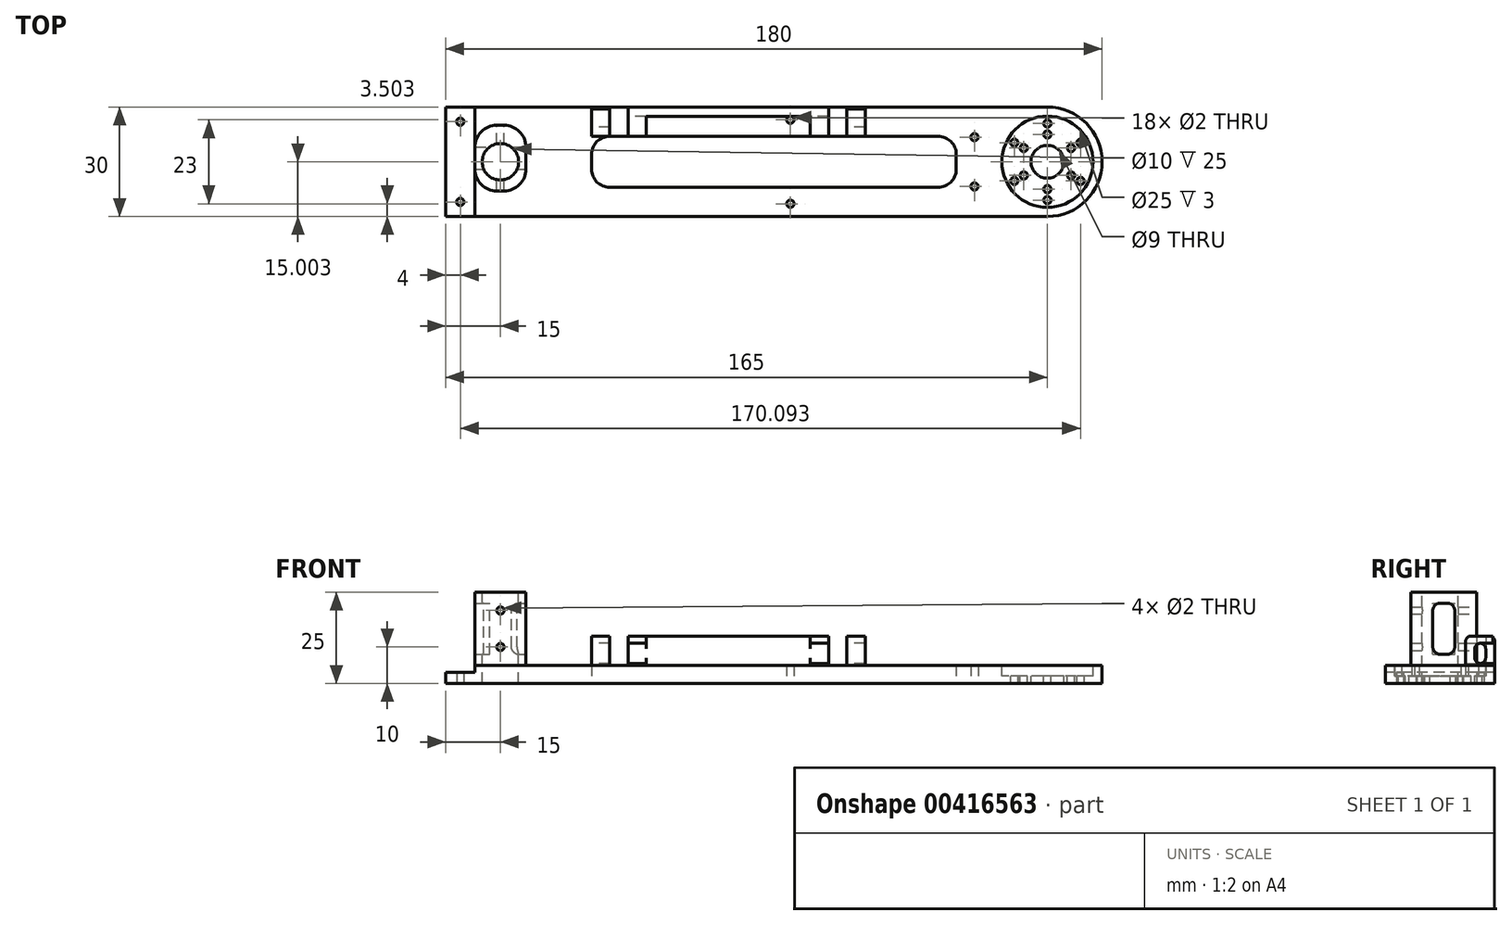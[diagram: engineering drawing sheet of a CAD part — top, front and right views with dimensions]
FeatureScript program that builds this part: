
annotation { "Feature Type Name" : "Feature", "Feature Type Description" : "" }
export const myFeature = defineFeature(function(context is Context, id is Id, definition is map)
    precondition{}
    {
        {
            var Q0;
            Q0=qCreatedBy(makeId("Top.planeOp"),FACE);
            var sketch = newSketch(context, id + "F0", { "sketchPlane" : qUnion([Q0])});
            skLineSegment(sketch, "E0.bottom", {"start": v(-80, 3.1) * mm, "end": v(100, 3.1) * mm});
            skLineSegment(sketch, "E0.top", {"start": v(-80, -26.9) * mm, "end": v(100, -26.9) * mm});
            skLineSegment(sketch, "E0.left", {"start": v(-80, 3.1) * mm, "end": v(-80, -26.9) * mm});
            skLineSegment(sketch, "E0.right", {"start": v(100, 3.1) * mm, "end": v(100, -26.9) * mm});
            skCircle(sketch, "E1", {"center": v(65, -5.15) * mm, "radius": 1 * mm});
            skCircle(sketch, "E2", {"center": v(65, -18.65) * mm, "radius": 1 * mm});
            skLineSegment(sketch, "E3.bottom", {"start": v(-40, -4.9) * mm, "end": v(60, -4.9) * mm});
            skLineSegment(sketch, "E3.top", {"start": v(-40, -18.9) * mm, "end": v(60, -18.9) * mm});
            skLineSegment(sketch, "E3.left", {"start": v(-40, -4.9) * mm, "end": v(-40, -18.9) * mm});
            skLineSegment(sketch, "E3.right", {"start": v(60, -4.9) * mm, "end": v(60, -18.9) * mm});
            skCircle(sketch, "E4", {"center": v(-76, -0.9) * mm, "radius": 1 * mm});
            skCircle(sketch, "E5", {"center": v(-76, -22.9) * mm, "radius": 1 * mm});
            skCircle(sketch, "E6", {"center": v(14.5, -23.4) * mm, "radius": 1 * mm});
            skCircle(sketch, "E7", {"center": v(14.5, -0.4) * mm, "radius": 1 * mm});
            skSolve(sketch);
        }
        {
            var Q0;
            Q0=makeQuery(id+"F0.imprint","IMPRINT",FACE,{"disambiguationData":[TD([[makeQuery(id+"F0.imprint","IMPRINT",EDGE,{"derivedFrom":sQuery(id+"F0.wireOp",EDGE,"E0.bottom")}),-1.0]])]});
            extrude(context, id + "F1", {"entities" : qUnion([Q0]), "depth" : 5 * mm});
        }
        {
            var Q0;
            Q0=makeQuery(id+"F1.opExtrude","CAP_FACE",FACE,{"disambiguationData":[OSD([sQuery(id+"F0.wireOp",EDGE,"E0.bottom"),sQuery(id+"F0.wireOp",EDGE,"E0.top"),sQuery(id+"F0.wireOp",EDGE,"E0.left"),sQuery(id+"F0.wireOp",EDGE,"E0.right")])],"isStart":false});
            var sketch = newSketch(context, id + "F2", { "sketchPlane" : qUnion([Q0])});
            skCircle(sketch, "E8", {"center": v(85, -11.9) * mm, "radius": 12.5 * mm});
            skCircle(sketch, "E9", {"center": v(85, -11.9) * mm, "radius": 4.5 * mm});
            skCircle(sketch, "E10", {"center": v(85, -4.4) * mm, "radius": 1 * mm});
            skCircle(sketch, "E11", {"center": v(85, -19.4) * mm, "radius": 1 * mm});
            skCircle(sketch, "E12", {"center": v(-65, -11.9) * mm, "radius": 5 * mm});
            skLineSegment(sketch, "E13.bottom", {"start": v(-72, -1.9) * mm, "end": v(-58, -1.9) * mm});
            skLineSegment(sketch, "E13.top", {"start": v(-72, -19.9) * mm, "end": v(-58, -19.9) * mm});
            skLineSegment(sketch, "E13.left", {"start": v(-72, -1.9) * mm, "end": v(-72, -19.9) * mm});
            skLineSegment(sketch, "E13.right", {"start": v(-58, -1.9) * mm, "end": v(-58, -19.9) * mm});
            skLineSegment(sketch, "E14.bottom", {"start": v(-80, 3.1) * mm, "end": v(-72, 3.1) * mm});
            skLineSegment(sketch, "E14.top", {"start": v(-80, -26.9) * mm, "end": v(-72, -26.9) * mm});
            skLineSegment(sketch, "E14.left", {"start": v(-80, 3.1) * mm, "end": v(-80, -26.9) * mm});
            skLineSegment(sketch, "E14.right", {"start": v(-72, 3.1) * mm, "end": v(-72, -26.9) * mm});
            skLineSegment(sketch, "E15", {"start": v(85, -11.9) * mm, "end": v(98.65, -11.9) * mm, "construction": true});
            skLineSegment(sketch, "E16", {"start": v(85, -11.9) * mm, "end": v(96.98, -4.98) * mm, "construction": true});
            skLineSegment(sketch, "E17", {"start": v(85, -11.9) * mm, "end": v(73.1, -5.02) * mm, "construction": true});
            skLineSegment(sketch, "E18", {"start": v(85, -11.9) * mm, "end": v(97.19, -18.93) * mm, "construction": true});
            skLineSegment(sketch, "E19", {"start": v(85, -11.9) * mm, "end": v(72.98, -18.84) * mm, "construction": true});
            skCircle(sketch, "E20", {"center": v(91.5, -8.15) * mm, "radius": 1 * mm});
            skCircle(sketch, "E21", {"center": v(91.5, -15.65) * mm, "radius": 1 * mm});
            skCircle(sketch, "E22", {"center": v(78.5, -15.65) * mm, "radius": 1 * mm});
            skCircle(sketch, "E23", {"center": v(78.5, -8.15) * mm, "radius": 1 * mm});
            skLineSegment(sketch, "E24", {"start": v(85, -11.9) * mm, "end": v(85, -25.3) * mm, "construction": true});
            skLineSegment(sketch, "E25", {"start": v(85, -11.9) * mm, "end": v(85, 1.9) * mm, "construction": true});
            skCircle(sketch, "E26", {"center": v(85, -1.4) * mm, "radius": 1 * mm});
            skCircle(sketch, "E27", {"center": v(85, -22.4) * mm, "radius": 1 * mm});
            skCircle(sketch, "E28", {"center": v(94.1, -17.15) * mm, "radius": 1 * mm});
            skCircle(sketch, "E29", {"center": v(94.1, -6.65) * mm, "radius": 1 * mm});
            skCircle(sketch, "E30", {"center": v(75.9, -6.65) * mm, "radius": 1 * mm});
            skCircle(sketch, "E31", {"center": v(75.9, -17.15) * mm, "radius": 1 * mm});
            skSolve(sketch);
        }
        {
            var Q0;
            Q0=makeQuery(id+"F2.imprint","IMPRINT",FACE,{"disambiguationData":[TD([[makeQuery(id+"F2.imprint","IMPRINT",EDGE,{"derivedFrom":sQuery(id+"F2.wireOp",EDGE,"E8")}),1.0]])]});
            extrude(context, id + "F3", {"entities" : qUnion([Q0]), "operationType" : NewBodyOperationType.REMOVE, "oppositeDirection" : true, "depth" : 3 * mm});
        }
        {
            var Q0;
            Q0=makeQuery(id+"F2.imprint","IMPRINT",FACE,{"disambiguationData":[TD([[makeQuery(id+"F2.imprint","IMPRINT",EDGE,{"derivedFrom":sQuery(id+"F2.wireOp",EDGE,"E9")}),1.0]])]});
            var Q1;
            Q1=makeQuery(id+"F2.imprint","IMPRINT",FACE,{"disambiguationData":[TD([[makeQuery(id+"F2.imprint","IMPRINT",EDGE,{"derivedFrom":sQuery(id+"F2.wireOp",EDGE,"E10")}),1.0]])]});
            var Q2;
            Q2=makeQuery(id+"F2.imprint","IMPRINT",FACE,{"disambiguationData":[TD([[makeQuery(id+"F2.imprint","IMPRINT",EDGE,{"derivedFrom":sQuery(id+"F2.wireOp",EDGE,"5qcmUWc9-dUiE-HqhH-y48y-BH5WIywJNnlC")}),1.0]])]});
            var Q3;
            Q3=makeQuery(id+"F2.imprint","IMPRINT",FACE,{"disambiguationData":[TD([[makeQuery(id+"F2.imprint","IMPRINT",EDGE,{"derivedFrom":sQuery(id+"F2.wireOp",EDGE,"E11")}),1.0]])]});
            var Q4;
            Q4=makeQuery(id+"F2.imprint","IMPRINT",FACE,{"disambiguationData":[TD([[makeQuery(id+"F2.imprint","IMPRINT",EDGE,{"derivedFrom":sQuery(id+"F2.wireOp",EDGE,"wZEUfmAI-Y2Ez-LQvS-xFHq-oZ12hOKPTyTT")}),1.0]])]});
            var Q5;
            Q5=makeQuery(id+"F2.imprint","IMPRINT",FACE,{"disambiguationData":[TD([[makeQuery(id+"F2.imprint","IMPRINT",EDGE,{"derivedFrom":sQuery(id+"F2.wireOp",EDGE,"E20")}),1.0]])]});
            var Q6;
            Q6=makeQuery(id+"F2.imprint","IMPRINT",FACE,{"disambiguationData":[TD([[makeQuery(id+"F2.imprint","IMPRINT",EDGE,{"derivedFrom":sQuery(id+"F2.wireOp",EDGE,"E21")}),1.0]])]});
            var Q7;
            Q7=makeQuery(id+"F2.imprint","IMPRINT",FACE,{"disambiguationData":[TD([[makeQuery(id+"F2.imprint","IMPRINT",EDGE,{"derivedFrom":sQuery(id+"F2.wireOp",EDGE,"E22")}),1.0]])]});
            var Q8;
            Q8=makeQuery(id+"F2.imprint","IMPRINT",FACE,{"disambiguationData":[TD([[makeQuery(id+"F2.imprint","IMPRINT",EDGE,{"derivedFrom":sQuery(id+"F2.wireOp",EDGE,"E23")}),1.0]])]});
            var Q9;
            Q9=makeQuery(id+"F2.imprint","IMPRINT",FACE,{"disambiguationData":[TD([[makeQuery(id+"F2.imprint","IMPRINT",EDGE,{"derivedFrom":sQuery(id+"F2.wireOp",EDGE,"E26")}),1.0]])]});
            var Q10;
            Q10=makeQuery(id+"F2.imprint","IMPRINT",FACE,{"disambiguationData":[TD([[makeQuery(id+"F2.imprint","IMPRINT",EDGE,{"derivedFrom":sQuery(id+"F2.wireOp",EDGE,"E30")}),1.0]])]});
            var Q11;
            Q11=makeQuery(id+"F2.imprint","IMPRINT",FACE,{"disambiguationData":[TD([[makeQuery(id+"F2.imprint","IMPRINT",EDGE,{"derivedFrom":sQuery(id+"F2.wireOp",EDGE,"E31")}),1.0]])]});
            var Q12;
            Q12=makeQuery(id+"F2.imprint","IMPRINT",FACE,{"disambiguationData":[TD([[makeQuery(id+"F2.imprint","IMPRINT",EDGE,{"derivedFrom":sQuery(id+"F2.wireOp",EDGE,"E27")}),1.0]])]});
            var Q13;
            Q13=makeQuery(id+"F2.imprint","IMPRINT",FACE,{"disambiguationData":[TD([[makeQuery(id+"F2.imprint","IMPRINT",EDGE,{"derivedFrom":sQuery(id+"F2.wireOp",EDGE,"E28")}),1.0]])]});
            var Q14;
            Q14=makeQuery(id+"F2.imprint","IMPRINT",FACE,{"disambiguationData":[TD([[makeQuery(id+"F2.imprint","IMPRINT",EDGE,{"derivedFrom":sQuery(id+"F2.wireOp",EDGE,"E29")}),1.0]])]});
            extrude(context, id + "F4", {"entities" : qUnion([Q0, Q1, Q2, Q3, Q4, Q5, Q6, Q7, Q8, Q9, Q10, Q11, Q12, Q13, Q14]), "operationType" : NewBodyOperationType.REMOVE, "oppositeDirection" : true, "depth" : 25 * mm, "offsetDistance" : 25 * mm});
        }
        {
            var Q0;
            Q0=makeQuery(id+"F1.opExtrude","SWEPT_EDGE",EDGE,{"disambiguationData":[OSD([sQuery(id+"F0.wireOp",EDGE,"E0.bottom"),sQuery(id+"F0.wireOp",EDGE,"E0.right")])]});
            var Q1;
            Q1=makeQuery(id+"F1.opExtrude","SWEPT_EDGE",EDGE,{"disambiguationData":[OSD([sQuery(id+"F0.wireOp",EDGE,"E0.top"),sQuery(id+"F0.wireOp",EDGE,"E0.right")])]});
            fillet(context, id + "F5", {"entities" : qUnion([Q0, Q1]), "radius" : 15 * mm, "tangentPropagation" : true, "allowEdgeOverflow" : false});
        }
        {
            var Q0;
            Q0=makeQuery(id+"F2.imprint","IMPRINT",FACE,{"disambiguationData":[TD([[makeQuery(id+"F2.imprint","IMPRINT",EDGE,{"derivedFrom":sQuery(id+"F2.wireOp",EDGE,"E12")}),1.0]])]});
            extrude(context, id + "F6", {"entities" : qUnion([Q0]), "operationType" : NewBodyOperationType.REMOVE, "oppositeDirection" : true, "depth" : 25 * mm});
        }
        {
            var Q0;
            Q0=makeQuery(id+"F1.opExtrude","SWEPT_EDGE",EDGE,{"disambiguationData":[OSD([sQuery(id+"F0.wireOp",EDGE,"E3.bottom"),sQuery(id+"F0.wireOp",EDGE,"E3.left")])]});
            var Q1;
            Q1=makeQuery(id+"F1.opExtrude","SWEPT_EDGE",EDGE,{"disambiguationData":[OSD([sQuery(id+"F0.wireOp",EDGE,"E3.top"),sQuery(id+"F0.wireOp",EDGE,"E3.left")])]});
            var Q2;
            Q2=makeQuery(id+"F1.opExtrude","SWEPT_EDGE",EDGE,{"disambiguationData":[OSD([sQuery(id+"F0.wireOp",EDGE,"E3.bottom"),sQuery(id+"F0.wireOp",EDGE,"E3.right")])]});
            var Q3;
            Q3=makeQuery(id+"F1.opExtrude","SWEPT_EDGE",EDGE,{"disambiguationData":[OSD([sQuery(id+"F0.wireOp",EDGE,"E3.top"),sQuery(id+"F0.wireOp",EDGE,"E3.right")])]});
            fillet(context, id + "F7", {"entities" : qUnion([Q0, Q1, Q2, Q3]), "radius" : 5 * mm, "tangentPropagation" : true, "allowEdgeOverflow" : false});
        }
        {
            var Q0;
            Q0=makeQuery(id+"F2.imprint","IMPRINT",FACE,{"disambiguationData":[TD([[makeQuery(id+"F2.imprint","IMPRINT",EDGE,{"derivedFrom":sQuery(id+"F2.wireOp",EDGE,"E12")}),-1.0]])]});
            extrude(context, id + "F8", {"entities" : qUnion([Q0]), "operationType" : NewBodyOperationType.ADD, "depth" : 20 * mm, "offsetDistance" : 25 * mm});
        }
        {
            var Q0;
            Q0=makeQuery(id+"F8.opExtrude","SWEPT_EDGE",EDGE,{"disambiguationData":[OSD([sQuery(id+"F2.wireOp",EDGE,"E13.top"),sQuery(id+"F2.wireOp",EDGE,"E13.left")])]});
            var Q1;
            Q1=makeQuery(id+"F8.opExtrude","SWEPT_EDGE",EDGE,{"disambiguationData":[OSD([sQuery(id+"F2.wireOp",EDGE,"E13.top"),sQuery(id+"F2.wireOp",EDGE,"E13.right")])]});
            var Q2;
            Q2=makeQuery(id+"F8.opExtrude","SWEPT_EDGE",EDGE,{"disambiguationData":[OSD([sQuery(id+"F2.wireOp",EDGE,"E13.bottom"),sQuery(id+"F2.wireOp",EDGE,"E13.left")])]});
            var Q3;
            Q3=makeQuery(id+"F8.opExtrude","SWEPT_EDGE",EDGE,{"disambiguationData":[OSD([sQuery(id+"F2.wireOp",EDGE,"E13.bottom"),sQuery(id+"F2.wireOp",EDGE,"E13.right")])]});
            fillet(context, id + "F9", {"entities" : qUnion([Q0, Q1, Q2, Q3]), "radius" : 6 * mm, "tangentPropagation" : true, "allowEdgeOverflow" : false});
        }
        {
            var Q0;
            {var subQ2=sQuery(id+"F2.wireOp",EDGE,"E14.bottom");Q0=makeQuery(id+"F2.imprint","IMPRINT",FACE,{"disambiguationData":[TD([[makeQuery(id+"F2.imprint","IMPRINT",EDGE,{"derivedFrom":subQ2}),-1.0]])]});}
            extrude(context, id + "F10", {"entities" : qUnion([Q0]), "operationType" : NewBodyOperationType.REMOVE, "oppositeDirection" : true, "depth" : 2 * mm, "offsetDistance" : 25 * mm});
        }
        {
            var Q0;
            Q0=makeQuery(id+"F8.opExtrude","SWEPT_FACE",FACE,{"disambiguationData":[OSD([sQuery(id+"F2.wireOp",EDGE,"E13.right")])]});
            var sketch = newSketch(context, id + "F11", { "sketchPlane" : qUnion([Q0])});
            skLineSegment(sketch, "E32.bottom", {"start": v(-13.9, 22) * mm, "end": v(-7.9, 22) * mm});
            skLineSegment(sketch, "E32.top", {"start": v(-13.9, 8) * mm, "end": v(-7.9, 8) * mm});
            skLineSegment(sketch, "E32.left", {"start": v(-13.9, 22) * mm, "end": v(-13.9, 8) * mm});
            skLineSegment(sketch, "E32.right", {"start": v(-7.9, 22) * mm, "end": v(-7.9, 8) * mm});
            skSolve(sketch);
        }
        {
            var Q0;
            Q0=makeQuery(id+"F11.imprint","IMPRINT",FACE,{"disambiguationData":[TD([[makeQuery(id+"F11.imprint","IMPRINT",EDGE,{"derivedFrom":sQuery(id+"F11.wireOp",EDGE,"E32.bottom")}),-1.0]])]});
            extrude(context, id + "F12", {"entities" : qUnion([Q0]), "operationType" : NewBodyOperationType.REMOVE, "oppositeDirection" : true, "depth" : 25 * mm, "offsetDistance" : 25 * mm});
        }
        {
            var Q0;
            {var subQ0=sQuery(id+"F2.wireOp",EDGE,"E13.right");var subQ1=sQuery(id+"F2.wireOp",EDGE,"E13.top");var subQ3=sQuery(id+"F11.wireOp",EDGE,"E32.top");var subQ4=sQuery(id+"F11.wireOp",EDGE,"E32.left");Q0=makeQuery(id+"F12.boolean.opBoolean","COPY",EDGE,{"disambiguationData":[TD([makeQuery(id+"F8.opExtrude","SWEPT_FACE",FACE,{"disambiguationData":[OSD([subQ0])]})])],"derivedFrom":makeQuery(id+"F12.opExtrude","SWEPT_EDGE",EDGE,{"disambiguationData":[OSD([subQ1,subQ0,subQ3,subQ4])]})});}
            var Q1;
            {var subQ0=sQuery(id+"F2.wireOp",EDGE,"E13.right");var subQ2=sQuery(id+"F2.wireOp",EDGE,"E13.bottom");var subQ3=sQuery(id+"F11.wireOp",EDGE,"E32.top");var subQ4=sQuery(id+"F11.wireOp",EDGE,"E32.right");Q1=makeQuery(id+"F12.boolean.opBoolean","COPY",EDGE,{"disambiguationData":[TD([makeQuery(id+"F8.opExtrude","SWEPT_FACE",FACE,{"disambiguationData":[OSD([subQ0])]})])],"derivedFrom":makeQuery(id+"F12.opExtrude","SWEPT_EDGE",EDGE,{"disambiguationData":[OSD([subQ2,subQ0,subQ3,subQ4])]})});}
            var Q2;
            {var subQ0=sQuery(id+"F2.wireOp",EDGE,"E13.right");var subQ2=sQuery(id+"F2.wireOp",EDGE,"E13.bottom");var subQ3=sQuery(id+"F11.wireOp",EDGE,"E32.bottom");var subQ4=sQuery(id+"F11.wireOp",EDGE,"E32.right");Q2=makeQuery(id+"F12.boolean.opBoolean","COPY",EDGE,{"disambiguationData":[TD([makeQuery(id+"F8.opExtrude","SWEPT_FACE",FACE,{"disambiguationData":[OSD([subQ0])]})])],"derivedFrom":makeQuery(id+"F12.opExtrude","SWEPT_EDGE",EDGE,{"disambiguationData":[OSD([subQ2,subQ0,subQ3,subQ4])]})});}
            var Q3;
            {var subQ0=sQuery(id+"F2.wireOp",EDGE,"E13.right");var subQ1=sQuery(id+"F2.wireOp",EDGE,"E13.top");var subQ3=sQuery(id+"F11.wireOp",EDGE,"E32.bottom");var subQ4=sQuery(id+"F11.wireOp",EDGE,"E32.left");Q3=makeQuery(id+"F12.boolean.opBoolean","COPY",EDGE,{"disambiguationData":[TD([makeQuery(id+"F8.opExtrude","SWEPT_FACE",FACE,{"disambiguationData":[OSD([subQ0])]})])],"derivedFrom":makeQuery(id+"F12.opExtrude","SWEPT_EDGE",EDGE,{"disambiguationData":[OSD([subQ1,subQ0,subQ3,subQ4])]})});}
            var Q4;
            {var subQ0=sQuery(id+"F2.wireOp",EDGE,"E14.right");var subQ1=sQuery(id+"F2.wireOp",EDGE,"E13.top");var subQ2=sQuery(id+"F11.wireOp",EDGE,"E32.top");var subQ4=sQuery(id+"F11.wireOp",EDGE,"E32.left");Q4=makeQuery(id+"F12.boolean.opBoolean","COPY",EDGE,{"disambiguationData":[TD([makeQuery(id+"F8.opExtrude","SWEPT_FACE",FACE,{"disambiguationData":[OSD([subQ0])]})])],"derivedFrom":makeQuery(id+"F12.opExtrude","SWEPT_EDGE",EDGE,{"disambiguationData":[OSD([subQ1,sQuery(id+"F2.wireOp",EDGE,"E13.right"),subQ2,subQ4])]})});}
            var Q5;
            {var subQ0=sQuery(id+"F2.wireOp",EDGE,"E14.right");var subQ1=sQuery(id+"F2.wireOp",EDGE,"E13.bottom");var subQ2=sQuery(id+"F11.wireOp",EDGE,"E32.right");var subQ3=sQuery(id+"F11.wireOp",EDGE,"E32.top");Q5=makeQuery(id+"F12.boolean.opBoolean","COPY",EDGE,{"disambiguationData":[TD([makeQuery(id+"F8.opExtrude","SWEPT_FACE",FACE,{"disambiguationData":[OSD([subQ0])]})])],"derivedFrom":makeQuery(id+"F12.opExtrude","SWEPT_EDGE",EDGE,{"disambiguationData":[OSD([subQ1,sQuery(id+"F2.wireOp",EDGE,"E13.right"),subQ3,subQ2])]})});}
            var Q6;
            {var subQ0=sQuery(id+"F2.wireOp",EDGE,"E14.right");var subQ1=sQuery(id+"F2.wireOp",EDGE,"E13.bottom");var subQ2=sQuery(id+"F11.wireOp",EDGE,"E32.right");var subQ4=sQuery(id+"F11.wireOp",EDGE,"E32.bottom");Q6=makeQuery(id+"F12.boolean.opBoolean","COPY",EDGE,{"disambiguationData":[TD([makeQuery(id+"F8.opExtrude","SWEPT_FACE",FACE,{"disambiguationData":[OSD([subQ0])]})])],"derivedFrom":makeQuery(id+"F12.opExtrude","SWEPT_EDGE",EDGE,{"disambiguationData":[OSD([subQ1,sQuery(id+"F2.wireOp",EDGE,"E13.right"),subQ4,subQ2])]})});}
            var Q7;
            {var subQ0=sQuery(id+"F2.wireOp",EDGE,"E14.right");var subQ1=sQuery(id+"F2.wireOp",EDGE,"E13.top");var subQ3=sQuery(id+"F11.wireOp",EDGE,"E32.bottom");var subQ4=sQuery(id+"F11.wireOp",EDGE,"E32.left");Q7=makeQuery(id+"F12.boolean.opBoolean","COPY",EDGE,{"disambiguationData":[TD([makeQuery(id+"F8.opExtrude","SWEPT_FACE",FACE,{"disambiguationData":[OSD([subQ0])]})])],"derivedFrom":makeQuery(id+"F12.opExtrude","SWEPT_EDGE",EDGE,{"disambiguationData":[OSD([subQ1,sQuery(id+"F2.wireOp",EDGE,"E13.right"),subQ3,subQ4])]})});}
            fillet(context, id + "F13", {"entities" : qUnion([Q0, Q1, Q2, Q3, Q4, Q5, Q6, Q7]), "radius" : 2 * mm, "tangentPropagation" : true, "allowEdgeOverflow" : false});
        }
        {
            var Q0;
            Q0=makeQuery(id+"F8.opExtrude","SWEPT_FACE",FACE,{"disambiguationData":[OSD([sQuery(id+"F2.wireOp",EDGE,"E13.bottom")])]});
            var sketch = newSketch(context, id + "F14", { "sketchPlane" : qUnion([Q0])});
            skCircle(sketch, "E33", {"center": v(65, 20) * mm, "radius": 1 * mm});
            skCircle(sketch, "E34", {"center": v(65, 10) * mm, "radius": 1 * mm});
            skSolve(sketch);
        }
        {
            var Q0;
            {var subQ0=sQuery(id+"F14.wireOp",EDGE,"E33");var subQ1=sQuery(id+"F2.wireOp",EDGE,"E13.bottom");var subQ2=makeQuery(id+"F8.opExtrude","SWEPT_FACE",FACE,{"disambiguationData":[OSD([subQ1])]});var subQ3=makeQuery(id+"F14.imprint","INTERSECT",VERTEX,{"derivedFrom":[makeQuery(id+"F9.opFillet","BLEND_EDGE",EDGE,{"blendedFrom":[makeQuery(id+"F8.opExtrude","SWEPT_EDGE",EDGE,{"disambiguationData":[OSD([subQ1,sQuery(id+"F2.wireOp",EDGE,"E14.right")])]}),subQ2],"blendedInto":[subQ2]}),subQ0]});Q0=makeQuery(id+"F14.imprint","IMPRINT",FACE,{"disambiguationData":[TD([[makeQuery(id+"F14.imprint","IMPRINT",EDGE,{"disambiguationData":[TD([[subQ3,-1.0]])],"derivedFrom":subQ0}),1.0]])]});}
            var Q1;
            {var subQ0=sQuery(id+"F14.wireOp",EDGE,"E34");var subQ1=sQuery(id+"F2.wireOp",EDGE,"E13.bottom");var subQ2=makeQuery(id+"F8.opExtrude","SWEPT_FACE",FACE,{"disambiguationData":[OSD([subQ1])]});var subQ3=makeQuery(id+"F14.imprint","INTERSECT",VERTEX,{"derivedFrom":[makeQuery(id+"F9.opFillet","BLEND_EDGE",EDGE,{"blendedFrom":[makeQuery(id+"F8.opExtrude","SWEPT_EDGE",EDGE,{"disambiguationData":[OSD([subQ1,sQuery(id+"F2.wireOp",EDGE,"E14.right")])]}),subQ2],"blendedInto":[subQ2]}),subQ0]});Q1=makeQuery(id+"F14.imprint","IMPRINT",FACE,{"disambiguationData":[TD([[makeQuery(id+"F14.imprint","IMPRINT",EDGE,{"disambiguationData":[TD([[subQ3,-1.0]])],"derivedFrom":subQ0}),1.0]])]});}
            extrude(context, id + "F15", {"entities" : qUnion([Q0, Q1]), "operationType" : NewBodyOperationType.REMOVE, "oppositeDirection" : true, "depth" : 25 * mm, "offsetDistance" : 25 * mm});
        }
        {
            var Q0;
            Q0=makeQuery(id+"F2.imprint","IMPRINT",FACE,{"disambiguationData":[TD([[makeQuery(id+"F2.imprint","IMPRINT",EDGE,{"derivedFrom":sQuery(id+"F2.wireOp",EDGE,"E8")}),-1.0]])]});
            var sketch = newSketch(context, id + "F16", { "sketchPlane" : qUnion([Q0])});
            skLineSegment(sketch, "E35.bottom", {"start": v(-40, 3.1) * mm, "end": v(-35, 3.1) * mm});
            skLineSegment(sketch, "E35.top", {"start": v(-40, -4.9) * mm, "end": v(-35, -4.9) * mm});
            skLineSegment(sketch, "E35.left", {"start": v(-40, 3.1) * mm, "end": v(-40, -4.9) * mm});
            skLineSegment(sketch, "E35.right", {"start": v(-35, 3.1) * mm, "end": v(-35, -4.9) * mm});
            skLineSegment(sketch, "E36.bottom", {"start": v(-30, 3.1) * mm, "end": v(-25, 3.1) * mm});
            skLineSegment(sketch, "E36.top", {"start": v(-30, -4.9) * mm, "end": v(-25, -4.9) * mm});
            skLineSegment(sketch, "E36.left", {"start": v(-30, 3.1) * mm, "end": v(-30, -4.9) * mm});
            skLineSegment(sketch, "E36.right", {"start": v(-25, 3.1) * mm, "end": v(-25, -4.9) * mm});
            skLineSegment(sketch, "E37.bottom", {"start": v(20, 3.1) * mm, "end": v(25, 3.1) * mm});
            skLineSegment(sketch, "E37.top", {"start": v(20, -4.9) * mm, "end": v(25, -4.9) * mm});
            skLineSegment(sketch, "E37.left", {"start": v(20, 3.1) * mm, "end": v(20, -4.9) * mm});
            skLineSegment(sketch, "E37.right", {"start": v(25, 3.1) * mm, "end": v(25, -4.9) * mm});
            skLineSegment(sketch, "E38.bottom", {"start": v(30, 3.1) * mm, "end": v(35, 3.1) * mm});
            skLineSegment(sketch, "E38.top", {"start": v(30, -4.9) * mm, "end": v(35, -4.9) * mm});
            skLineSegment(sketch, "E38.left", {"start": v(30, 3.1) * mm, "end": v(30, -4.9) * mm});
            skLineSegment(sketch, "E38.right", {"start": v(35, 3.1) * mm, "end": v(35, -4.9) * mm});
            skLineSegment(sketch, "E39.bottom", {"start": v(-25, 3.1) * mm, "end": v(20, 3.1) * mm});
            skLineSegment(sketch, "E39.top", {"start": v(-25, 0.6) * mm, "end": v(20, 0.6) * mm});
            skLineSegment(sketch, "E39.left", {"start": v(-25, 3.1) * mm, "end": v(-25, 0.6) * mm});
            skLineSegment(sketch, "E39.right", {"start": v(20, 3.1) * mm, "end": v(20, 0.6) * mm});
            skSolve(sketch);
        }
        {
            var Q0;
            Q0=makeQuery(id+"F16.imprint","IMPRINT",FACE,{"disambiguationData":[TD([[makeQuery(id+"F16.imprint","IMPRINT",EDGE,{"derivedFrom":sQuery(id+"F16.wireOp",EDGE,"E35.bottom")}),-1.0]])]});
            var Q1;
            Q1=makeQuery(id+"F16.imprint","IMPRINT",FACE,{"disambiguationData":[TD([[makeQuery(id+"F16.imprint","IMPRINT",EDGE,{"derivedFrom":sQuery(id+"F16.wireOp",EDGE,"E36.bottom")}),-1.0]])]});
            var Q2;
            Q2=makeQuery(id+"F16.imprint","IMPRINT",FACE,{"disambiguationData":[TD([[makeQuery(id+"F16.imprint","IMPRINT",EDGE,{"derivedFrom":sQuery(id+"F16.wireOp",EDGE,"E37.bottom")}),-1.0]])]});
            var Q3;
            Q3=makeQuery(id+"F16.imprint","IMPRINT",FACE,{"disambiguationData":[TD([[makeQuery(id+"F16.imprint","IMPRINT",EDGE,{"derivedFrom":sQuery(id+"F16.wireOp",EDGE,"E38.bottom")}),-1.0]])]});
            extrude(context, id + "F17", {"entities" : qUnion([Q0, Q1, Q2, Q3]), "operationType" : NewBodyOperationType.ADD, "depth" : 8 * mm, "offsetDistance" : 25 * mm});
        }
        {
            var Q0;
            Q0=makeQuery(id+"F17.opExtrude","SWEPT_FACE",FACE,{"disambiguationData":[OSD([sQuery(id+"F16.wireOp",EDGE,"E35.left")])]});
            var sketch = newSketch(context, id + "F18", { "sketchPlane" : qUnion([Q0])});
            skLineSegment(sketch, "E40.bottom", {"start": v(-3.1, 11) * mm, "end": v(2.4, 11) * mm});
            skLineSegment(sketch, "E40.top", {"start": v(-3.1, 5.5) * mm, "end": v(2.4, 5.5) * mm});
            skLineSegment(sketch, "E40.left", {"start": v(-3.1, 11) * mm, "end": v(-3.1, 5.5) * mm});
            skLineSegment(sketch, "E40.right", {"start": v(2.4, 11) * mm, "end": v(2.4, 5.5) * mm});
            skSolve(sketch);
        }
        {
            var Q0;
            Q0=makeQuery(id+"F17.opExtrude","SWEPT_FACE",FACE,{"disambiguationData":[OSD([sQuery(id+"F16.wireOp",EDGE,"E36.left")])]});
            var sketch = newSketch(context, id + "F19", { "sketchPlane" : qUnion([Q0])});
            skLineSegment(sketch, "E41.bottom", {"start": v(4.9, 11) * mm, "end": v(-0.6, 11) * mm});
            skLineSegment(sketch, "E41.top", {"start": v(4.9, 5.5) * mm, "end": v(-0.6, 5.5) * mm});
            skLineSegment(sketch, "E41.left", {"start": v(4.9, 11) * mm, "end": v(4.9, 5.5) * mm});
            skLineSegment(sketch, "E41.right", {"start": v(-0.6, 11) * mm, "end": v(-0.6, 5.5) * mm});
            skSolve(sketch);
        }
        {
            var Q0;
            Q0=makeQuery(id+"F17.opExtrude","SWEPT_FACE",FACE,{"disambiguationData":[OSD([sQuery(id+"F16.wireOp",EDGE,"E37.left")])]});
            var sketch = newSketch(context, id + "F20", { "sketchPlane" : qUnion([Q0])});
            skLineSegment(sketch, "E42.bottom", {"start": v(4.9, 11) * mm, "end": v(-0.6, 11) * mm});
            skLineSegment(sketch, "E42.top", {"start": v(4.9, 5.5) * mm, "end": v(-0.6, 5.5) * mm});
            skLineSegment(sketch, "E42.left", {"start": v(4.9, 11) * mm, "end": v(4.9, 5.5) * mm});
            skLineSegment(sketch, "E42.right", {"start": v(-0.6, 11) * mm, "end": v(-0.6, 5.5) * mm});
            skSolve(sketch);
        }
        {
            var Q0;
            Q0=makeQuery(id+"F17.opExtrude","SWEPT_FACE",FACE,{"disambiguationData":[OSD([sQuery(id+"F16.wireOp",EDGE,"E38.left")])]});
            var sketch = newSketch(context, id + "F21", { "sketchPlane" : qUnion([Q0])});
            skLineSegment(sketch, "E43.bottom", {"start": v(-3.1, 11) * mm, "end": v(2.4, 11) * mm});
            skLineSegment(sketch, "E43.top", {"start": v(-3.1, 5.5) * mm, "end": v(2.4, 5.5) * mm});
            skLineSegment(sketch, "E43.left", {"start": v(-3.1, 11) * mm, "end": v(-3.1, 5.5) * mm});
            skLineSegment(sketch, "E43.right", {"start": v(2.4, 11) * mm, "end": v(2.4, 5.5) * mm});
            skSolve(sketch);
        }
        {
            var Q0;
            Q0=makeQuery(id+"F18.imprint","IMPRINT",FACE,{"disambiguationData":[TD([[makeQuery(id+"F18.imprint","IMPRINT",EDGE,{"derivedFrom":sQuery(id+"F18.wireOp",EDGE,"E40.bottom")}),-1.0]])]});
            var Q1;
            Q1=makeQuery(id+"F19.imprint","IMPRINT",FACE,{"disambiguationData":[TD([[makeQuery(id+"F19.imprint","IMPRINT",EDGE,{"derivedFrom":sQuery(id+"F19.wireOp",EDGE,"E41.bottom")}),1.0]])]});
            var Q2;
            Q2=makeQuery(id+"F20.imprint","IMPRINT",FACE,{"disambiguationData":[TD([[makeQuery(id+"F20.imprint","IMPRINT",EDGE,{"derivedFrom":sQuery(id+"F20.wireOp",EDGE,"E42.bottom")}),1.0]])]});
            var Q3;
            Q3=makeQuery(id+"F21.imprint","IMPRINT",FACE,{"disambiguationData":[TD([[makeQuery(id+"F21.imprint","IMPRINT",EDGE,{"derivedFrom":sQuery(id+"F21.wireOp",EDGE,"E43.bottom")}),-1.0]])]});
            extrude(context, id + "F22", {"entities" : qUnion([Q0, Q1, Q2, Q3]), "operationType" : NewBodyOperationType.REMOVE, "oppositeDirection" : true, "depth" : 6 * mm, "offsetDistance" : 25 * mm});
        }
        {
            var Q0;
            Q0=makeQuery(id+"F16.imprint","IMPRINT",FACE,{"disambiguationData":[TD([[makeQuery(id+"F16.imprint","IMPRINT",EDGE,{"derivedFrom":sQuery(id+"F16.wireOp",EDGE,"fd6NqXke-As7v-4CXU-9Ryy-qk9NiAzUaoPO.bottom")}),-1.0]])]});
            var Q1;
            Q1=makeQuery(id+"F16.imprint","IMPRINT",FACE,{"disambiguationData":[TD([[makeQuery(id+"F16.imprint","IMPRINT",EDGE,{"derivedFrom":sQuery(id+"F16.wireOp",EDGE,"E39.bottom")}),-1.0]])]});
            extrude(context, id + "F23", {"entities" : qUnion([Q0, Q1]), "operationType" : NewBodyOperationType.ADD, "depth" : 8 * mm, "offsetDistance" : 25 * mm});
        }
        {
            var Q0;
            {var subQ2=sQuery(id+"F16.wireOp",EDGE,"E38.bottom");Q0=makeQuery(id+"F22.boolean.opBoolean","SPLIT",FACE,{"disambiguationData":[TD([makeQuery(id+"F22.opExtrude","SWEPT_FACE",FACE,{"disambiguationData":[OSD([sQuery(id+"F21.wireOp",EDGE,"E43.bottom")])]})])],"derivedFrom":makeQuery(id+"F17.boolean.opBoolean","MERGE",FACE,{"derivedFrom":[makeQuery(id+"F1.opExtrude","SWEPT_FACE",FACE,{"disambiguationData":[OSD([sQuery(id+"F0.wireOp",EDGE,"E0.bottom")])]}),makeQuery(id+"F17.opExtrude","SWEPT_FACE",FACE,{"disambiguationData":[OSD([sQuery(id+"F16.wireOp",EDGE,"E35.bottom")])]}),makeQuery(id+"F17.opExtrude","SWEPT_FACE",FACE,{"disambiguationData":[OSD([sQuery(id+"F16.wireOp",EDGE,"E36.bottom")])]}),makeQuery(id+"F17.opExtrude","SWEPT_FACE",FACE,{"disambiguationData":[OSD([sQuery(id+"F16.wireOp",EDGE,"E37.bottom")])]}),makeQuery(id+"F17.opExtrude","SWEPT_FACE",FACE,{"disambiguationData":[OSD([subQ2])]})]})});}
            var Q1;
            {var subQ3=sQuery(id+"F16.wireOp",EDGE,"E37.top");Q1=makeQuery(id+"F22.boolean.opBoolean","SPLIT",FACE,{"disambiguationData":[TD([makeQuery(id+"F22.opExtrude","SWEPT_FACE",FACE,{"disambiguationData":[OSD([sQuery(id+"F20.wireOp",EDGE,"E42.bottom")])]})])],"derivedFrom":makeQuery(id+"F17.boolean.opBoolean","MERGE",FACE,{"derivedFrom":[makeQuery(id+"F1.opExtrude","SWEPT_FACE",FACE,{"disambiguationData":[OSD([sQuery(id+"F0.wireOp",EDGE,"E3.bottom")])]}),makeQuery(id+"F17.opExtrude","SWEPT_FACE",FACE,{"disambiguationData":[OSD([sQuery(id+"F16.wireOp",EDGE,"E36.top")])]}),makeQuery(id+"F17.opExtrude","SWEPT_FACE",FACE,{"disambiguationData":[OSD([subQ3])]}),makeQuery(id+"F17.opExtrude","SWEPT_FACE",FACE,{"disambiguationData":[OSD([sQuery(id+"F16.wireOp",EDGE,"E38.top")])]})]})});}
            var Q2;
            {var subQ3=sQuery(id+"F16.wireOp",EDGE,"E36.top");Q2=makeQuery(id+"F22.boolean.opBoolean","SPLIT",FACE,{"disambiguationData":[TD([makeQuery(id+"F22.opExtrude","SWEPT_FACE",FACE,{"disambiguationData":[OSD([sQuery(id+"F19.wireOp",EDGE,"E41.bottom")])]})])],"derivedFrom":makeQuery(id+"F17.boolean.opBoolean","MERGE",FACE,{"derivedFrom":[makeQuery(id+"F1.opExtrude","SWEPT_FACE",FACE,{"disambiguationData":[OSD([sQuery(id+"F0.wireOp",EDGE,"E3.bottom")])]}),makeQuery(id+"F17.opExtrude","SWEPT_FACE",FACE,{"disambiguationData":[OSD([subQ3])]}),makeQuery(id+"F17.opExtrude","SWEPT_FACE",FACE,{"disambiguationData":[OSD([sQuery(id+"F16.wireOp",EDGE,"E37.top")])]}),makeQuery(id+"F17.opExtrude","SWEPT_FACE",FACE,{"disambiguationData":[OSD([sQuery(id+"F16.wireOp",EDGE,"E38.top")])]})]})});}
            var Q3;
            {var subQ2=sQuery(id+"F16.wireOp",EDGE,"E35.bottom");Q3=makeQuery(id+"F22.boolean.opBoolean","SPLIT",FACE,{"disambiguationData":[TD([makeQuery(id+"F22.opExtrude","SWEPT_FACE",FACE,{"disambiguationData":[OSD([sQuery(id+"F18.wireOp",EDGE,"E40.bottom")])]})])],"derivedFrom":makeQuery(id+"F17.boolean.opBoolean","MERGE",FACE,{"derivedFrom":[makeQuery(id+"F1.opExtrude","SWEPT_FACE",FACE,{"disambiguationData":[OSD([sQuery(id+"F0.wireOp",EDGE,"E0.bottom")])]}),makeQuery(id+"F17.opExtrude","SWEPT_FACE",FACE,{"disambiguationData":[OSD([subQ2])]}),makeQuery(id+"F17.opExtrude","SWEPT_FACE",FACE,{"disambiguationData":[OSD([sQuery(id+"F16.wireOp",EDGE,"E36.bottom")])]}),makeQuery(id+"F17.opExtrude","SWEPT_FACE",FACE,{"disambiguationData":[OSD([sQuery(id+"F16.wireOp",EDGE,"E37.bottom")])]}),makeQuery(id+"F17.opExtrude","SWEPT_FACE",FACE,{"disambiguationData":[OSD([sQuery(id+"F16.wireOp",EDGE,"E38.bottom")])]})]})});}
            extrude(context, id + "F24", {"entities" : qUnion([Q0, Q1, Q2, Q3]), "operationType" : NewBodyOperationType.REMOVE, "oppositeDirection" : true, "depth" : 0.5 * mm, "offsetDistance" : 25 * mm});
        }
        {
            var Q0;
            Q0=makeQuery(id+"F17.opExtrude","CAP_EDGE",EDGE,{"disambiguationData":[OSD([sQuery(id+"F16.wireOp",EDGE,"E35.bottom")])],"isStart":false});
            var Q1;
            Q1=makeQuery(id+"F17.opExtrude","CAP_EDGE",EDGE,{"disambiguationData":[OSD([sQuery(id+"F16.wireOp",EDGE,"E36.bottom")])],"isStart":false});
            var Q2;
            Q2=makeQuery(id+"F22.boolean.opBoolean","COPY",EDGE,{"derivedFrom":makeQuery(id+"F22.opExtrude","SWEPT_EDGE",EDGE,{"disambiguationData":[OSD([sQuery(id+"F19.wireOp",EDGE,"vCpt7z00-XQ2m-L6Kx-0X8V-3utIlPoUw3UM.top"),sQuery(id+"F19.wireOp",EDGE,"vCpt7z00-XQ2m-L6Kx-0X8V-3utIlPoUw3UM.right")])]})});
            var Q3;
            Q3=makeQuery(id+"F22.boolean.opBoolean","COPY",EDGE,{"derivedFrom":makeQuery(id+"F22.opExtrude","SWEPT_EDGE",EDGE,{"disambiguationData":[OSD([sQuery(id+"F19.wireOp",EDGE,"vCpt7z00-XQ2m-L6Kx-0X8V-3utIlPoUw3UM.bottom"),sQuery(id+"F19.wireOp",EDGE,"vCpt7z00-XQ2m-L6Kx-0X8V-3utIlPoUw3UM.right")])]})});
            var Q4;
            Q4=makeQuery(id+"F17.opExtrude","CAP_EDGE",EDGE,{"disambiguationData":[OSD([sQuery(id+"F16.wireOp",EDGE,"E35.top")])],"isStart":false});
            var Q5;
            Q5=makeQuery(id+"F22.boolean.opBoolean","COPY",EDGE,{"derivedFrom":makeQuery(id+"F22.opExtrude","SWEPT_EDGE",EDGE,{"disambiguationData":[OSD([sQuery(id+"F18.wireOp",EDGE,"xJFCYaTs-IYRT-QUAs-stMh-C4VbORP7GGMH.top"),sQuery(id+"F18.wireOp",EDGE,"xJFCYaTs-IYRT-QUAs-stMh-C4VbORP7GGMH.right")])]})});
            var Q6;
            Q6=makeQuery(id+"F22.boolean.opBoolean","COPY",EDGE,{"derivedFrom":makeQuery(id+"F22.opExtrude","SWEPT_EDGE",EDGE,{"disambiguationData":[OSD([sQuery(id+"F18.wireOp",EDGE,"xJFCYaTs-IYRT-QUAs-stMh-C4VbORP7GGMH.bottom"),sQuery(id+"F18.wireOp",EDGE,"xJFCYaTs-IYRT-QUAs-stMh-C4VbORP7GGMH.right")])]})});
            var Q7;
            Q7=makeQuery(id+"F17.opExtrude","CAP_EDGE",EDGE,{"disambiguationData":[OSD([sQuery(id+"F16.wireOp",EDGE,"E36.top")])],"isStart":false});
            var Q8;
            Q8=makeQuery(id+"F22.boolean.opBoolean","COPY",EDGE,{"derivedFrom":makeQuery(id+"F22.opExtrude","SWEPT_EDGE",EDGE,{"disambiguationData":[OSD([sQuery(id+"F20.wireOp",EDGE,"Ap48zGqF-vmaS-oI5a-AC55-ZimYdizw6Qxy.top"),sQuery(id+"F20.wireOp",EDGE,"Ap48zGqF-vmaS-oI5a-AC55-ZimYdizw6Qxy.right")])]})});
            var Q9;
            Q9=makeQuery(id+"F17.opExtrude","CAP_EDGE",EDGE,{"disambiguationData":[OSD([sQuery(id+"F16.wireOp",EDGE,"E37.bottom")])],"isStart":false});
            var Q10;
            Q10=makeQuery(id+"F22.boolean.opBoolean","COPY",EDGE,{"derivedFrom":makeQuery(id+"F22.opExtrude","SWEPT_EDGE",EDGE,{"disambiguationData":[OSD([sQuery(id+"F20.wireOp",EDGE,"Ap48zGqF-vmaS-oI5a-AC55-ZimYdizw6Qxy.bottom"),sQuery(id+"F20.wireOp",EDGE,"Ap48zGqF-vmaS-oI5a-AC55-ZimYdizw6Qxy.right")])]})});
            var Q11;
            Q11=makeQuery(id+"F17.opExtrude","CAP_EDGE",EDGE,{"disambiguationData":[OSD([sQuery(id+"F16.wireOp",EDGE,"E37.top")])],"isStart":false});
            var Q12;
            Q12=makeQuery(id+"F17.opExtrude","CAP_EDGE",EDGE,{"disambiguationData":[OSD([sQuery(id+"F16.wireOp",EDGE,"E38.bottom")])],"isStart":false});
            var Q13;
            Q13=makeQuery(id+"F17.opExtrude","CAP_EDGE",EDGE,{"disambiguationData":[OSD([sQuery(id+"F16.wireOp",EDGE,"E38.top")])],"isStart":false});
            var Q14;
            Q14=makeQuery(id+"F22.boolean.opBoolean","COPY",EDGE,{"derivedFrom":makeQuery(id+"F22.opExtrude","SWEPT_EDGE",EDGE,{"disambiguationData":[OSD([sQuery(id+"F21.wireOp",EDGE,"vG7Bm0Yc-fvpn-7uIM-Jf4p-eSzZdNbD0F9Y.top"),sQuery(id+"F21.wireOp",EDGE,"vG7Bm0Yc-fvpn-7uIM-Jf4p-eSzZdNbD0F9Y.right")])]})});
            var Q15;
            Q15=makeQuery(id+"F22.boolean.opBoolean","COPY",EDGE,{"derivedFrom":makeQuery(id+"F22.opExtrude","SWEPT_EDGE",EDGE,{"disambiguationData":[OSD([sQuery(id+"F21.wireOp",EDGE,"vG7Bm0Yc-fvpn-7uIM-Jf4p-eSzZdNbD0F9Y.bottom"),sQuery(id+"F21.wireOp",EDGE,"vG7Bm0Yc-fvpn-7uIM-Jf4p-eSzZdNbD0F9Y.right")])]})});
            var Q16;
            Q16=makeQuery(id+"F22.boolean.opBoolean","COPY",EDGE,{"derivedFrom":makeQuery(id+"F22.opExtrude","SWEPT_EDGE",EDGE,{"disambiguationData":[OSD([sQuery(id+"F21.wireOp",EDGE,"E43.bottom"),sQuery(id+"F21.wireOp",EDGE,"E43.right")])]})});
            var Q17;
            Q17=makeQuery(id+"F22.boolean.opBoolean","COPY",EDGE,{"derivedFrom":makeQuery(id+"F22.opExtrude","SWEPT_EDGE",EDGE,{"disambiguationData":[OSD([sQuery(id+"F21.wireOp",EDGE,"E43.top"),sQuery(id+"F21.wireOp",EDGE,"E43.right")])]})});
            var Q18;
            Q18=makeQuery(id+"F22.boolean.opBoolean","COPY",EDGE,{"derivedFrom":makeQuery(id+"F22.opExtrude","SWEPT_EDGE",EDGE,{"disambiguationData":[OSD([sQuery(id+"F18.wireOp",EDGE,"E40.top"),sQuery(id+"F18.wireOp",EDGE,"E40.right")])]})});
            var Q19;
            Q19=makeQuery(id+"F22.boolean.opBoolean","COPY",EDGE,{"derivedFrom":makeQuery(id+"F22.opExtrude","SWEPT_EDGE",EDGE,{"disambiguationData":[OSD([sQuery(id+"F18.wireOp",EDGE,"E40.bottom"),sQuery(id+"F18.wireOp",EDGE,"E40.right")])]})});
            var Q20;
            Q20=makeQuery(id+"F22.boolean.opBoolean","COPY",EDGE,{"derivedFrom":makeQuery(id+"F22.opExtrude","SWEPT_EDGE",EDGE,{"disambiguationData":[OSD([sQuery(id+"F19.wireOp",EDGE,"E41.top"),sQuery(id+"F19.wireOp",EDGE,"E41.right")])]})});
            var Q21;
            Q21=makeQuery(id+"F22.boolean.opBoolean","COPY",EDGE,{"derivedFrom":makeQuery(id+"F22.opExtrude","SWEPT_EDGE",EDGE,{"disambiguationData":[OSD([sQuery(id+"F20.wireOp",EDGE,"E42.top"),sQuery(id+"F20.wireOp",EDGE,"E42.right")])]})});
            var Q22;
            Q22=makeQuery(id+"F22.boolean.opBoolean","COPY",EDGE,{"derivedFrom":makeQuery(id+"F22.opExtrude","SWEPT_EDGE",EDGE,{"disambiguationData":[OSD([sQuery(id+"F19.wireOp",EDGE,"E41.bottom"),sQuery(id+"F19.wireOp",EDGE,"E41.right")])]})});
            var Q23;
            Q23=makeQuery(id+"F22.boolean.opBoolean","COPY",EDGE,{"derivedFrom":makeQuery(id+"F22.opExtrude","SWEPT_EDGE",EDGE,{"disambiguationData":[OSD([sQuery(id+"F20.wireOp",EDGE,"E42.bottom"),sQuery(id+"F20.wireOp",EDGE,"E42.right")])]})});
            var Q24;
            Q24=makeQuery(id+"F24.boolean.opBoolean","COPY",EDGE,{"derivedFrom":makeQuery(id+"F24.opExtrude","CAP_EDGE",EDGE,{"disambiguationData":[OSD([sQuery(id+"F16.wireOp",EDGE,"E35.bottom")])],"isStart":false})});
            var Q25;
            Q25=makeQuery(id+"F24.boolean.opBoolean","COPY",EDGE,{"derivedFrom":makeQuery(id+"F24.opExtrude","CAP_EDGE",EDGE,{"disambiguationData":[OSD([sQuery(id+"F16.wireOp",EDGE,"E38.bottom")])],"isStart":false})});
            fillet(context, id + "F25", {"entities" : qUnion([Q0, Q1, Q2, Q3, Q4, Q5, Q6, Q7, Q8, Q9, Q10, Q11, Q12, Q13, Q14, Q15, Q16, Q17, Q18, Q19, Q20, Q21, Q22, Q23, Q24, Q25]), "radius" : 1.5 * mm, "tangentPropagation" : true, "allowEdgeOverflow" : false});
        }
    });
